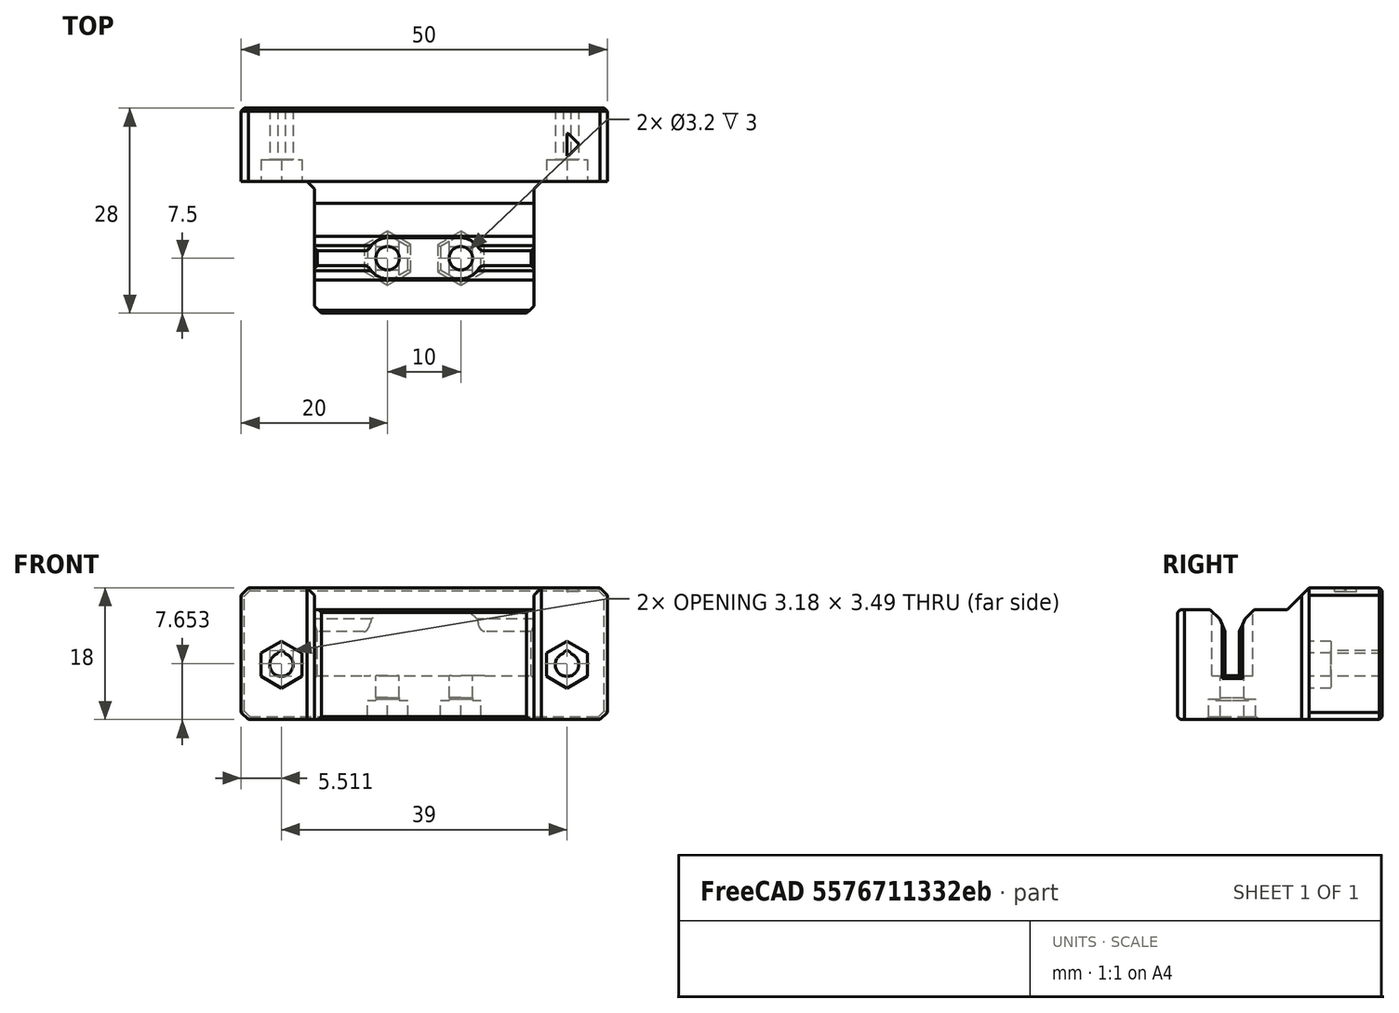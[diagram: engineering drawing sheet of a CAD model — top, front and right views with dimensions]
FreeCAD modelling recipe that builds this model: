
FCSTD DOCUMENT  (FreeCAD 0.18R14555 (Git shallow))
Label: y-belt-holder-100-lower
License: All rights reserved
LicenseURL: http://en.wikipedia.org/wiki/All_rights_reserved
objects: Part::MultiFuse×13, Part::Cylinder×8, Part::Feature×8, Part::Chamfer×8, Part::Box×6, Part::Cut×4, Part::Fillet×1
note: 48 computed .brp shape members not serialized (recipe doc carries the construction recipe); baked Part::Feature solids carry a one-line shape summary decoded from their .brp

FEATURE [Part::Box] Box  label="Cube"
  AttacherType = Attacher::AttachEngine3D
  Height = 18
  Length = 50
  Placement = pos=(-25,-10,0) rot=(0,0,1;0rad)
  Width = 10
FEATURE [Part::Box] Box001  label="Cube001"
  AttacherType = Attacher::AttachEngine3D
  Height = 15
  Length = 30
  Placement = pos=(-15,-28,0) rot=(0,0,1;0rad)
  Width = 28
FEATURE [Part::Box] Box002  label="Cube002"
  AttacherType = Attacher::AttachEngine3D
  Height = 12
  Length = 12
  Placement = pos=(3,-21.5,6) rot=(0,0,1;0rad)
  Width = 2
FEATURE [Part::Cylinder] Cylinder
  Angle = 360
  AttacherType = Attacher::AttachEngine3D
  Height = 18
  Placement = pos=(-5,-20.5,0) rot=(0,0,1;0rad)
  Radius = 1.6
FEATURE [Part::Box] Box003  label="Cube003"
  AttacherType = Attacher::AttachEngine3D
  Height = 12
  Length = 12
  Placement = pos=(-15,-21.5,6) rot=(0,0,1;0rad)
  Width = 2
FEATURE [Part::Cylinder] Cylinder004
  Angle = 360
  AttacherType = Attacher::AttachEngine3D
  Height = 18
  Placement = pos=(5,-20.5,0) rot=(0,0,1;0rad)
  Radius = 1.6
FEATURE [Part::Cylinder] Cylinder006
  Angle = 360
  AttacherType = Attacher::AttachEngine3D
  Height = 12
  Placement = pos=(5,-20.5,6) rot=(0,0,1;0rad)
  Radius = 2.8
FEATURE [Part::Cylinder] Cylinder007
  Angle = 360
  AttacherType = Attacher::AttachEngine3D
  Height = 12
  Placement = pos=(-5,-20.5,6) rot=(0,0,1;0rad)
  Radius = 2.8
FEATURE [Part::Box] Box004  label="Cube004"
  AttacherType = Attacher::AttachEngine3D
  Height = 12
  Length = 10
  Placement = pos=(-5,-23.3,6) rot=(0,0,1;0rad)
  Width = 5.6
FEATURE [Part::Cylinder] Cylinder008
  Angle = 360
  AttacherType = Attacher::AttachEngine3D
  Height = 18
  Placement = pos=(-19.5,1.7e-15,7.5) rot=(1,0,0;1.5708rad)
  Radius = 1.6
FEATURE [Part::Cylinder] Cylinder009
  Angle = 360
  AttacherType = Attacher::AttachEngine3D
  Height = 18
  Placement = pos=(19.5,1.7e-15,7.5) rot=(1,0,0;1.5708rad)
  Radius = 1.6
FEATURE [Part::MultiFuse] Fusion
  Shapes = -> [Cylinder,Cylinder004]
FEATURE [Part::MultiFuse] Fusion001
  Shapes = -> [Box002,Box003]
FEATURE [Part::MultiFuse] Fusion002
  Shapes = -> [Cylinder006,Cylinder007,Box004]
FEATURE [Part::MultiFuse] Fusion003
  Shapes = -> [Fusion002,Fusion001,Fusion]
FEATURE [Part::MultiFuse] Fusion005
  Shapes = -> [Cylinder008,Cylinder009]
FEATURE [Part::Feature] Body001
  Placement = pos=(-19.5,0,7.5) rot=(0,0,1;0rad)
  shape: bbox 5.543 x 3 x 6.4 mm, 8 faces (baked)
FEATURE [Part::Feature] Body002
  Placement = pos=(19.5,0,7.5) rot=(0,0,1;0rad)
  shape: bbox 5.543 x 3 x 6.4 mm, 8 faces (baked)
FEATURE [Part::MultiFuse] Fusion006
  Placement = pos=(0,-7,0) rot=(0,0,1;0rad)
  Shapes = -> [Body002,Body001]
FEATURE [Part::Cylinder] Cylinder010
  Angle = 360
  AttacherType = Attacher::AttachEngine3D
  Height = 10
  Placement = pos=(-19.5,1.7e-15,7.5) rot=(1,0,0;1.5708rad)
  Radius = 0.5
FEATURE [Part::Cylinder] Cylinder011
  Angle = 360
  AttacherType = Attacher::AttachEngine3D
  Height = 10
  Placement = pos=(19.5,2e-15,7.5) rot=(1,0,0;1.5708rad)
  Radius = 0.5
FEATURE [Part::MultiFuse] Fusion007
  Placement = pos=(0,0,1.4) rot=(0,0,1;0rad)
  Shapes = -> [Cylinder010,Cylinder011]
FEATURE [Part::Feature] Body003
  Placement = pos=(-5,-20.5,0) rot=(0,0,1;0rad)
  shape: bbox 5.543 x 6.4 x 3 mm, 8 faces (baked)
FEATURE [Part::Feature] Fusion008001  label="Fusion009"
  Placement = pos=(5,-20.5,0) rot=(0,0,1;0rad)
  shape: bbox 6 x 6.4 x 0.4 mm, 36 faces (baked)
FEATURE [Part::Feature] Body004
  Placement = pos=(5,-20.5,0) rot=(0,0,1;0rad)
  shape: bbox 5.543 x 6.4 x 3 mm, 8 faces (baked)
FEATURE [Part::Feature] Fusion008003  label="Fusion011"
  Placement = pos=(-5,-20.5,0) rot=(0,0,1;0rad)
  shape: bbox 6 x 6.4 x 0.4 mm, 36 faces (baked)
FEATURE [Part::MultiFuse] Fusion008004
  Placement = pos=(0,0,2.6) rot=(0,0,1;0rad)
  Shapes = -> [Fusion008003,Fusion008001]
FEATURE [Part::MultiFuse] Fusion008005
  Shapes = -> [Body004,Body003]
FEATURE [Part::MultiFuse] Fusion008006  label="mounting-screw"
  Shapes = -> [Fusion005,Fusion006,Fusion007]
FEATURE [Part::MultiFuse] Fusion008007
  Shapes = -> [Box,Box001]
FEATURE [Part::Cut] Cut
  Base = -> Fusion008007
  Tool = -> Fusion008006
FEATURE [Part::Cut] Cut001
  Base = -> Cut
  Tool = -> Fusion003
FEATURE [Part::Cut] Cut002
  Base = -> Cut001
  Tool = -> Fusion008005
FEATURE [Part::MultiFuse] Fusion008008
  Shapes = -> [Cut002,Fusion008004]
FEATURE [Part::Box] Box005  label="Cube005"
  AttacherType = Attacher::AttachEngine3D
  Height = 0.5
  Length = 1.6
  Placement = pos=(0,4,0) rot=(0,0,1;0rad)
  Width = 3
FEATURE [Part::Chamfer] Chamfer  label="indicator"
  Base = -> Box005
  Edges = 2 edges r=1.4: [Edge5,Edge7]
  Placement = pos=(19.5,-10.5,17.5) rot=(0,0,1;0rad)
FEATURE [Part::Feature] Pad001
  Placement = pos=(-15,2,-3) rot=(0.57735,0.57735,0.57735;2.0944rad)
  shape: bbox 30 x 3 x 3 mm, 5 faces (baked)
FEATURE [Part::Cut] Cut003
  Base = -> Fusion008008
  Tool = -> Chamfer
FEATURE [Part::MultiFuse] Fusion008009
  Shapes = -> [Cut003,Pad001]
FEATURE [Part::Chamfer] Chamfer001
  Base = -> Fusion008009
  Edges = 2 edges r=2: [Edge11,Edge93]
FEATURE [Part::Chamfer] Chamfer002
  Base = -> Chamfer001
  Edges = 2 edges r=1: [Edge18,Edge37]
FEATURE [Part::Chamfer] Chamfer003
  Base = -> Chamfer002
  Edges = 2 edges r=1: [Edge19,Edge64]
FEATURE [Part::Fillet] Fillet
  Base = -> Chamfer003
  Edges = 4 edges r=1: [Edge26,Edge43,Edge64,Edge90]
FEATURE [Part::Chamfer] Chamfer004
  Base = -> Fillet
  Edges = 6 edges r=0.4: [Edge7,Edge14,Edge16,Edge83,Edge84,Edge85]
FEATURE [Part::Chamfer] Chamfer005
  Base = -> Chamfer004
  Edges = 6 edges r=1: [Edge18,Edge45,Edge163,Edge164,Edge166,Edge228]
FEATURE [Part::Feature] Chamfer005001  label="Chamfer006"
  shape: bbox 50 x 28 x 18 mm, 109 faces (baked)
FEATURE [Part::Chamfer] Chamfer005002
  Base = -> Chamfer005001
  Edges = 22 edges r=0.4: [Edge4,Edge49,Edge82,Edge84,Edge86,Edge87,Edge146,Edge167,Edge168,Edge192,Edge193,Edge194,Edge195,Edge196,Edge197,Edge198,Edge199,Edge200,Edge201,Edge202,Edge203,Edge204]
FEATURE [Part::Chamfer] Chamfer005003
  Base = -> Chamfer005002
  Edges = 2 edges r=1: [Edge23,Edge36]
